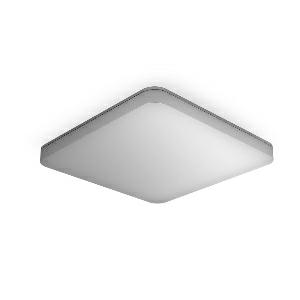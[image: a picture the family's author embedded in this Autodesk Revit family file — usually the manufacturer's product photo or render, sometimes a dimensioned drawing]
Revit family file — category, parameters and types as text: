
# Revit family: rs_pro_connect_r20_q_sl_057176
name_source: partatom
category: Leuchten
revit_build: Autodesk Revit 2016 (Build: 20190508_0715(x64)
units: mm (PartAtom-declared; Revit-internal decimal feet)

## family parameters
Basisbauteil = Fläche
Beim Laden mit Abzugskörper schneiden = Nein
Bemaßung runder Anschluss = Durchmesser verwenden
Gemeinsam genutzt = Nein
Lichtquelle = Nein
Raumberechnungspunkt = Nein
Teiletyp = Normal

## types (1)
- RS PRO Connect R20 Q SL (1 x , 1900 lm, 3000 K)
    Beschreibung = Dimensions (L x W x H): 55 x 300 x 300 mm; Mains power supply: 220 – 240 V / 50 – 60 Hz; Output: 16 W; Luminous flux: 1900 lm; Colour temperature: 3000 K; Colour variation LED: SDCM3; Colour Rendering Index CRI: 80-89; With lamp: Yes, STEINEL LED system; Lamp: LED cannot be replaced; LED life expectancy (max. °C): 50000 h; LED life expectancy (25 °C): 60000 h; Drop in luminous flux in accordance with LM80: L80B50; Base: without; LED cooling system: Passive Thermo Control; With motion detector: No; Main light adjustable: 50 - 100 %; Continuous light: selectable; Photo-cell controller: No; Basic light level function, detail: LED Backlight; Functions: Backlight; Soft light start: Yes; Impact resistance: IK07; IP-rating: IP40; Protection class: II; Ambient temperature: -20 – 40 °C; Housing material: Plastic; Cover material: PC, opal; Manufacturer's Warranty: 5 years; Settings via: Bluetooth; With remote control: No; Version: warm white; PU1, EAN: 4007841057176
    CIE Flux Codes = 44 75 93 94 100
    Color Rendering = 80-89
    Color Temperature = 3000 K
    Frequency = 60 Hz, 50 Hz
    Height = 300 mm
    Hersteller = Steinel
    Lamp Light Flux = 1900 lm
    Lamp count = 1
    Lampe = 1 x
    Length = 55 mm
    Luminous efficacy = 0 lm/W
    ModVariant = Nein
    Modell = 057176
    Mounting Type = Surface mounted
    Number of Poles = 1
    OnlyDefault = Ja
    Power Factor = 1
    Product Name = RS PRO Connect R20 Q SL
    Product group = Sensor-switched indoor light
    ProductGroupID = 30
    Protection Class = Protection class II
    Protection Degree = IP 40
    RlxData = <blob elided: 173937 chars, md5=985acaeb>
    Scheinlast = 0 VA
    Socket = socket
    Standby Power = 0 W
    System Light Flux = 0 lm
    System Power = 0 W
    Typenbild = produkt1_057176.jpg
    Typenkommentare = Product without accessories
    URL = http://relux.com
    VarID = ---
    Voltage = 0 V
    Vorgabe-Ansicht = 1800 mm
    Weight = 0.00 kg
    Width = 300 mm

## geometry (parser evidence)
native form markers: Sweep x13
no freeform markers — native parametric forms only
